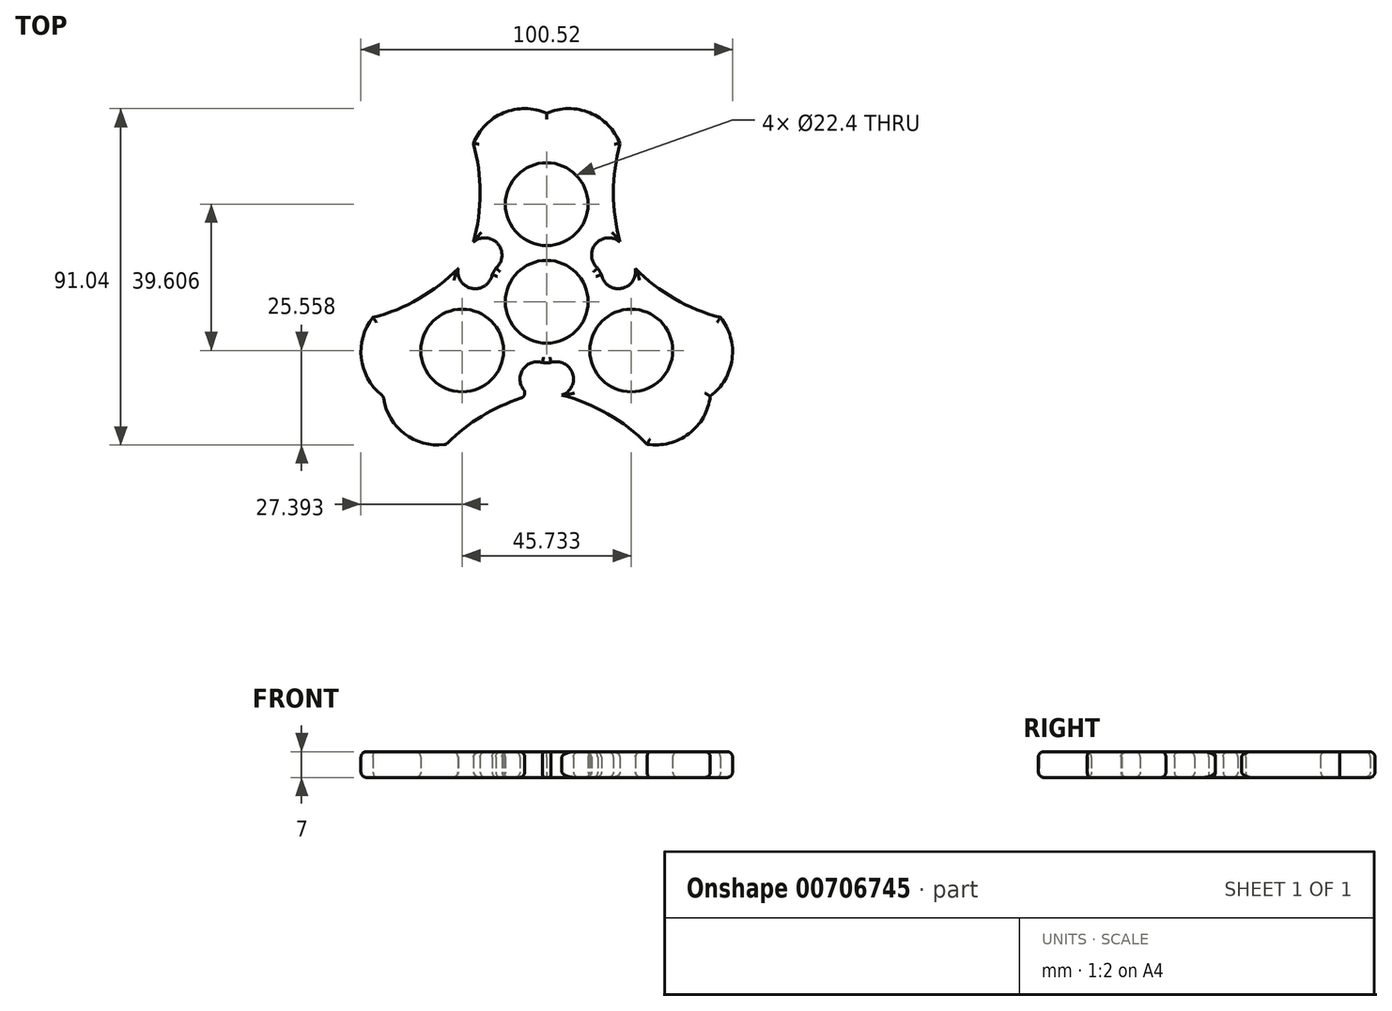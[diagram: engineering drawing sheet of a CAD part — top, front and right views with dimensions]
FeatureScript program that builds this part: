
annotation { "Feature Type Name" : "Feature", "Feature Type Description" : "" }
export const myFeature = defineFeature(function(context is Context, id is Id, definition is map)
    precondition{}
    {
        {
            var Q0;
            Q0=qCreatedBy(makeId("Top.planeOp"),FACE);
            var sketch = newSketch(context, id + "F0", { "sketchPlane" : qUnion([Q0])});
            skCircle(sketch, "E0", {"center": v(0, 0) * mm, "radius": 11.2 * mm});
            skArc(sketch, "E1", {"start": v(-2.9, -16.24) * mm, "mid": v(0, -16.5) * mm, "end": v(2.9, -16.24) * mm});
            skCircle(sketch, "E2", {"center": v(0, 26.4) * mm, "radius": 11.2 * mm});
            skCircle(sketch, "E3.1.1", {"center": v(-22.87, -13.2) * mm, "radius": 11.2 * mm});
            skCircle(sketch, "E3.2.1", {"center": v(22.87, -13.2) * mm, "radius": 11.2 * mm});
            skArc(sketch, "E4", {"start": v(0, 51.05) * mm, "mid": v(-11.67, 51.13) * mm, "end": v(-19.82, 42.77) * mm});
            skArc(sketch, "E5", {"start": v(-19.82, 16.17) * mm, "mid": v(-18.01, 29.47) * mm, "end": v(-19.82, 42.77) * mm});
            skArc(sketch, "E6", {"start": v(-13.77, 9.1) * mm, "mid": v(-13.24, 15.67) * mm, "end": v(-19.82, 16.17) * mm});
            skArc(sketch, "E7.MirrorCS", {"start": v(0, 51.05) * mm, "mid": v(11.67, 51.13) * mm, "end": v(19.82, 42.77) * mm});
            skArc(sketch, "E8.MirrorCS", {"start": v(19.82, 16.17) * mm, "mid": v(18.01, 29.47) * mm, "end": v(19.82, 42.77) * mm});
            skArc(sketch, "E9.MirrorCS", {"start": v(13.77, 9.1) * mm, "mid": v(13.24, 15.67) * mm, "end": v(19.82, 16.17) * mm});
            skArc(sketch, "E10.1.0", {"start": v(-23.94, 9.04) * mm, "mid": v(-34.55, 0.83) * mm, "end": v(-46.98, -4.26) * mm});
            skArc(sketch, "E10.1.1", {"start": v(-44.23, -25.56) * mm, "mid": v(-50.13, -15.5) * mm, "end": v(-46.98, -4.26) * mm});
            skArc(sketch, "E10.1.2", {"start": v(-44.23, -25.56) * mm, "mid": v(-38.46, -35.7) * mm, "end": v(-27.15, -38.6) * mm});
            skArc(sketch, "E10.1.3", {"start": v(-4.12, -25.3) * mm, "mid": v(-16.54, -30.37) * mm, "end": v(-27.15, -38.6) * mm});
            skArc(sketch, "E10.1.4", {"start": v(-1.01, -16.5) * mm, "mid": v(-6.97, -19.34) * mm, "end": v(-4.12, -25.3) * mm});
            skArc(sketch, "E10.1.5", {"start": v(-14.78, 7.34) * mm, "mid": v(-20.21, 3.6) * mm, "end": v(-23.94, 9.04) * mm});
            skArc(sketch, "E10.2.0", {"start": v(4.12, -25.29) * mm, "mid": v(16.54, -30.37) * mm, "end": v(27.15, -38.6) * mm});
            skArc(sketch, "E10.2.1", {"start": v(44.23, -25.56) * mm, "mid": v(38.46, -35.7) * mm, "end": v(27.15, -38.6) * mm});
            skArc(sketch, "E10.2.2", {"start": v(44.23, -25.56) * mm, "mid": v(50.13, -15.5) * mm, "end": v(46.98, -4.26) * mm});
            skArc(sketch, "E10.2.3", {"start": v(23.94, 9.04) * mm, "mid": v(34.55, 0.83) * mm, "end": v(46.98, -4.26) * mm});
            skArc(sketch, "E10.2.4", {"start": v(14.78, 7.34) * mm, "mid": v(20.22, 3.6) * mm, "end": v(23.94, 9.04) * mm});
            skArc(sketch, "E10.2.5", {"start": v(1.01, -16.5) * mm, "mid": v(6.97, -19.34) * mm, "end": v(4.12, -25.29) * mm});
            skPoint(sketch, "E10.center", {"position": v(0, -0.02) * mm});
            skArc(sketch, "E11.trimOffspring", {"start": v(15.56, 5.48) * mm, "mid": v(14.3, 8.24) * mm, "end": v(12.54, 10.73) * mm});
            skArc(sketch, "E12.trimOffspring", {"start": v(-12.54, 10.73) * mm, "mid": v(-14.3, 8.24) * mm, "end": v(-15.56, 5.48) * mm});
            skSolve(sketch);
        }
        {
            var Q0;
            Q0=makeQuery(id+"F0.imprint","IMPRINT",FACE,{"disambiguationData":[TD([[makeQuery(id+"F0.imprint","IMPRINT",EDGE,{"derivedFrom":sQuery(id+"F0.wireOp",EDGE,"E0")}),-1.0]])]});
            extrude(context, id + "F1", {"entities" : qUnion([Q0]), "depth" : 7 * mm, "offsetDistance" : 25 * mm});
        }
        {
            var Q0;
            Q0=makeQuery(id+"F1.opExtrude","CAP_EDGE",EDGE,{"disambiguationData":[OSD([sQuery(id+"F0.wireOp",EDGE,"E10.2.1")])],"isStart":true});
            var Q1;
            Q1=makeQuery(id+"F1.opExtrude","CAP_EDGE",EDGE,{"disambiguationData":[OSD([sQuery(id+"F0.wireOp",EDGE,"E10.2.2")])],"isStart":false});
            var Q2;
            Q2=makeQuery(id+"F1.opExtrude","CAP_FACE",FACE,{"disambiguationData":[OSD([sQuery(id+"F0.wireOp",EDGE,"E0"),sQuery(id+"F0.wireOp",EDGE,"E1"),sQuery(id+"F0.wireOp",EDGE,"E2"),sQuery(id+"F0.wireOp",EDGE,"E3.1.1"),sQuery(id+"F0.wireOp",EDGE,"E3.2.1"),sQuery(id+"F0.wireOp",EDGE,"E4"),sQuery(id+"F0.wireOp",EDGE,"E5"),sQuery(id+"F0.wireOp",EDGE,"E6"),sQuery(id+"F0.wireOp",EDGE,"E7.MirrorCS"),sQuery(id+"F0.wireOp",EDGE,"E8.MirrorCS"),sQuery(id+"F0.wireOp",EDGE,"E9.MirrorCS"),sQuery(id+"F0.wireOp",EDGE,"E10.1.0"),sQuery(id+"F0.wireOp",EDGE,"E10.1.1"),sQuery(id+"F0.wireOp",EDGE,"E10.1.2"),sQuery(id+"F0.wireOp",EDGE,"E10.1.3"),sQuery(id+"F0.wireOp",EDGE,"E10.1.4"),sQuery(id+"F0.wireOp",EDGE,"E10.1.5"),sQuery(id+"F0.wireOp",EDGE,"E10.2.0"),sQuery(id+"F0.wireOp",EDGE,"E10.2.1"),sQuery(id+"F0.wireOp",EDGE,"E10.2.2"),sQuery(id+"F0.wireOp",EDGE,"E10.2.3"),sQuery(id+"F0.wireOp",EDGE,"E10.2.4"),sQuery(id+"F0.wireOp",EDGE,"E10.2.5"),sQuery(id+"F0.wireOp",EDGE,"E11.trimOffspring"),sQuery(id+"F0.wireOp",EDGE,"E12.trimOffspring")])],"isStart":false});
            var Q3;
            Q3=makeQuery(id+"F1.opExtrude","SWEPT_FACE",FACE,{"disambiguationData":[OSD([sQuery(id+"F0.wireOp",EDGE,"E10.1.3")])]});
            var Q4;
            Q4=makeQuery(id+"F1.opExtrude","SWEPT_FACE",FACE,{"disambiguationData":[OSD([sQuery(id+"F0.wireOp",EDGE,"E10.1.2")])]});
            var Q5;
            Q5=makeQuery(id+"F1.opExtrude","CAP_FACE",FACE,{"disambiguationData":[OSD([sQuery(id+"F0.wireOp",EDGE,"E0"),sQuery(id+"F0.wireOp",EDGE,"E1"),sQuery(id+"F0.wireOp",EDGE,"E2"),sQuery(id+"F0.wireOp",EDGE,"E3.1.1"),sQuery(id+"F0.wireOp",EDGE,"E3.2.1"),sQuery(id+"F0.wireOp",EDGE,"E4"),sQuery(id+"F0.wireOp",EDGE,"E5"),sQuery(id+"F0.wireOp",EDGE,"E6"),sQuery(id+"F0.wireOp",EDGE,"E7.MirrorCS"),sQuery(id+"F0.wireOp",EDGE,"E8.MirrorCS"),sQuery(id+"F0.wireOp",EDGE,"E9.MirrorCS"),sQuery(id+"F0.wireOp",EDGE,"E10.1.0"),sQuery(id+"F0.wireOp",EDGE,"E10.1.1"),sQuery(id+"F0.wireOp",EDGE,"E10.1.2"),sQuery(id+"F0.wireOp",EDGE,"E10.1.3"),sQuery(id+"F0.wireOp",EDGE,"E10.1.4"),sQuery(id+"F0.wireOp",EDGE,"E10.1.5"),sQuery(id+"F0.wireOp",EDGE,"E10.2.0"),sQuery(id+"F0.wireOp",EDGE,"E10.2.1"),sQuery(id+"F0.wireOp",EDGE,"E10.2.2"),sQuery(id+"F0.wireOp",EDGE,"E10.2.3"),sQuery(id+"F0.wireOp",EDGE,"E10.2.4"),sQuery(id+"F0.wireOp",EDGE,"E10.2.5"),sQuery(id+"F0.wireOp",EDGE,"E11.trimOffspring"),sQuery(id+"F0.wireOp",EDGE,"E12.trimOffspring")])],"isStart":true});
            fillet(context, id + "F2", {"entities" : qUnion([Q0, Q1, Q2, Q3, Q4, Q5]), "radius" : 1.5 * mm, "tangentPropagation" : true, "allowEdgeOverflow" : false});
        }
    });
